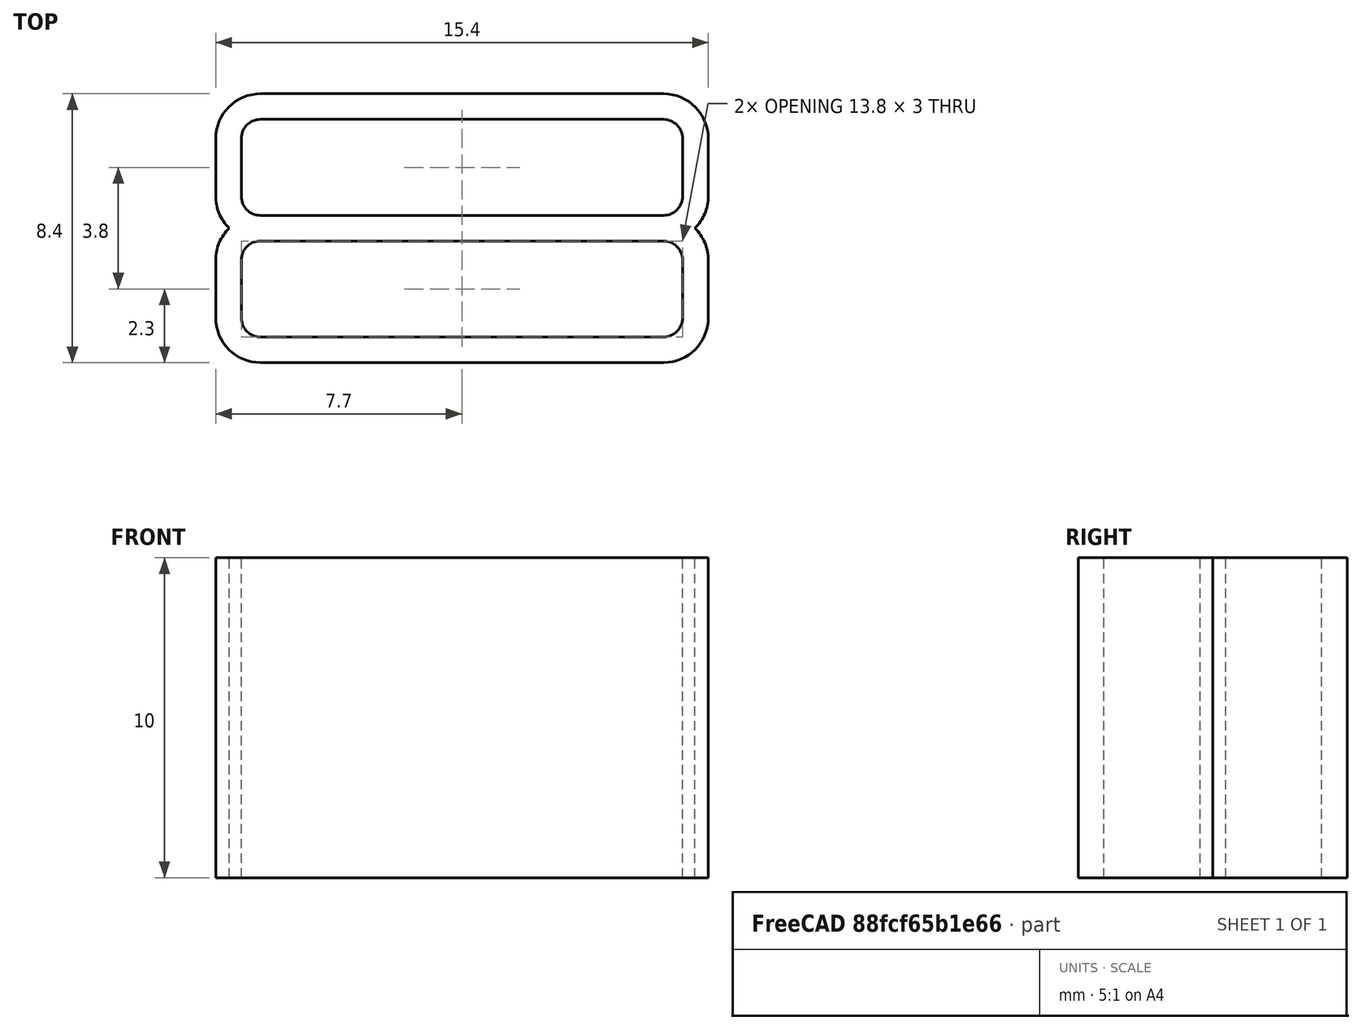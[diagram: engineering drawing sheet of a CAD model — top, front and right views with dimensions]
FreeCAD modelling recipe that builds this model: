
FCSTD DOCUMENT  (FreeCAD 1.0R39109 (Git))
Label: keeper
License: All rights reserved
LicenseURL: https://en.wikipedia.org/wiki/All_rights_reserved
objects: Sketcher::SketchObject×1, Spreadsheet::Sheet×1, PartDesign::Pad×1, PartDesign::Body×1
note: 6 computed .brp shape members not serialized (recipe doc carries the construction recipe); baked Part::Feature solids carry a one-line shape summary decoded from their .brp

FEATURE [Sketcher::SketchObject] Sketch
  ArcFitTolerance = 1e-06
  AttachmentSupport = -> [XY_Plane]
  FullyConstrained = true
  MakeInternals = false
  MapMode = 5
  expr: Constraints[39] = Spreadsheet.base_width
  expr: Constraints[43] = Spreadsheet.base_height
  expr: Constraints[46] = Spreadsheet.nozzle_width / 2
  expr: Constraints[50] = Spreadsheet.nozzle_width / 2
  expr: Constraints[59] = Spreadsheet.nozzle_width / 2
  expr: Constraints[60] = Spreadsheet.nozzle_width / 2
  expr: Constraints[61] = Spreadsheet.nozzle_width / 2
  expr: Constraints[62] = Spreadsheet.nozzle_width / 2
  sketch-geometry (78):
    g0: LineSegment [constr] StartX=-7.3 StartY=2.8 StartZ=0 EndX=-7.3 EndY=1 EndZ=0
    g1: LineSegment [constr] StartX=-6.3 StartY=0 StartZ=0 EndX=6.3 EndY=0 EndZ=0
    g2: LineSegment [constr] StartX=7.3 StartY=1 StartZ=0 EndX=7.3 EndY=2.8 EndZ=0
    g3: LineSegment [constr] StartX=6.3 StartY=3.8 StartZ=0 EndX=-6.3 EndY=3.8 EndZ=0
    g4: ArcOfCircle [constr] CenterX=-6.3 CenterY=2.8 CenterZ=0 NormalX=0 NormalY=0 NormalZ=1 AngleXU=0 Radius=1 StartAngle=1.5708 EndAngle=3.14159
    g5: ArcOfCircle [constr] CenterX=-6.3 CenterY=1 CenterZ=0 NormalX=0 NormalY=0 NormalZ=1 AngleXU=0 Radius=1 StartAngle=3.14159 EndAngle=4.71239
    g6: ArcOfCircle [constr] CenterX=6.3 CenterY=1 CenterZ=0 NormalX=0 NormalY=0 NormalZ=1 AngleXU=0 Radius=1 StartAngle=4.71239 EndAngle=6.28319
    g7: ArcOfCircle [constr] CenterX=6.3 CenterY=2.8 CenterZ=0 NormalX=0 NormalY=0 NormalZ=1 AngleXU=0 Radius=1 StartAngle=0 EndAngle=1.5708
    g8: GeomPoint [constr] X=-7.3 Y=3.8 Z=0
    g9: GeomPoint [constr] X=7.3 Y=0 Z=0
    g10: LineSegment [constr] StartX=-7.3 StartY=-1 StartZ=0 EndX=-7.3 EndY=-2.8 EndZ=0
    g11: LineSegment [constr] StartX=-6.3 StartY=-3.8 StartZ=0 EndX=6.3 EndY=-3.8 EndZ=0
    g12: LineSegment [constr] StartX=7.3 StartY=-2.8 StartZ=0 EndX=7.3 EndY=-1 EndZ=0
    g13: LineSegment [constr] StartX=6.3 StartY=0 StartZ=0 EndX=-6.3 EndY=0 EndZ=0
    g14: ArcOfCircle [constr] CenterX=-6.3 CenterY=-1 CenterZ=0 NormalX=0 NormalY=0 NormalZ=1 AngleXU=0 Radius=1 StartAngle=1.5708 EndAngle=3.14159
    g15: ArcOfCircle [constr] CenterX=-6.3 CenterY=-2.8 CenterZ=0 NormalX=0 NormalY=0 NormalZ=1 AngleXU=0 Radius=1 StartAngle=3.14159 EndAngle=4.71239
    g16: ArcOfCircle [constr] CenterX=6.3 CenterY=-2.8 CenterZ=0 NormalX=0 NormalY=0 NormalZ=1 AngleXU=0 Radius=1 StartAngle=4.71239 EndAngle=6.28319
    g17: ArcOfCircle [constr] CenterX=6.3 CenterY=-1 CenterZ=0 NormalX=0 NormalY=0 NormalZ=1 AngleXU=0 Radius=1 StartAngle=0 EndAngle=1.5708
    g18: GeomPoint [constr] X=-7.3 Y=0 Z=0
    g19: GeomPoint [constr] X=7.3 Y=-3.8 Z=0
    g20: LineSegment StartX=-6.3 StartY=4.2 StartZ=0 EndX=6.3 EndY=4.2 EndZ=0
    g21: LineSegment StartX=-6.3 StartY=3.4 StartZ=0 EndX=6.3 EndY=3.4 EndZ=0
    g22: LineSegment StartX=-6.3 StartY=0.4 StartZ=0 EndX=6.3 EndY=0.4 EndZ=0
    g23: LineSegment StartX=-6.3 StartY=-0.4 StartZ=0 EndX=6.3 EndY=-0.4 EndZ=0
    g24: LineSegment StartX=-6.3 StartY=-3.4 StartZ=0 EndX=6.3 EndY=-3.4 EndZ=0
    g25: LineSegment StartX=-6.3 StartY=-4.2 StartZ=0 EndX=6.3 EndY=-4.2 EndZ=0
    g26: LineSegment StartX=-7.7 StartY=2.8 StartZ=0 EndX=-7.7 EndY=1 EndZ=0
    g27: LineSegment StartX=-6.9 StartY=2.8 StartZ=0 EndX=-6.9 EndY=1 EndZ=0
    g28: LineSegment [constr] StartX=-7.7 StartY=2.8 StartZ=0 EndX=-6.9 EndY=2.8 EndZ=0
    g29: LineSegment [constr] StartX=-7.7 StartY=1 StartZ=0 EndX=-6.9 EndY=1 EndZ=0
    g30: ArcOfCircle CenterX=-6.3 CenterY=2.8 CenterZ=0 NormalX=0 NormalY=0 NormalZ=1 AngleXU=0 Radius=0.6 StartAngle=1.5708 EndAngle=3.14159
    g31: LineSegment [constr] StartX=-6.3 StartY=3.4 StartZ=0 EndX=-6.3 EndY=2.8 EndZ=0
    g32: LineSegment [constr] StartX=-6.9 StartY=2.8 StartZ=0 EndX=-6.3 EndY=2.8 EndZ=0
    g33: ArcOfCircle CenterX=-6.3 CenterY=1 CenterZ=0 NormalX=0 NormalY=0 NormalZ=1 AngleXU=0 Radius=0.6 StartAngle=3.14159 EndAngle=4.71239
    g34: LineSegment [constr] StartX=-6.3 StartY=1 StartZ=0 EndX=-6.3 EndY=0.4 EndZ=0
    g35: LineSegment [constr] StartX=-6.9 StartY=1 StartZ=0 EndX=-6.3 EndY=1 EndZ=0
    g36: ArcOfCircle CenterX=-6.3 CenterY=2.8 CenterZ=0 NormalX=0 NormalY=0 NormalZ=1 AngleXU=0 Radius=1.4 StartAngle=1.5708 EndAngle=3.14159
    g37: LineSegment [constr] StartX=-6.3 StartY=4.2 StartZ=0 EndX=-6.3 EndY=2.8 EndZ=0
    g38: LineSegment [constr] StartX=-7.7 StartY=2.8 StartZ=0 EndX=-6.3 EndY=2.8 EndZ=0
    g39: LineSegment StartX=-7.7 StartY=-1 StartZ=0 EndX=-7.7 EndY=-2.8 EndZ=0
    g40: LineSegment StartX=-6.9 StartY=-1 StartZ=0 EndX=-6.9 EndY=-2.8 EndZ=0
    g41: LineSegment [constr] StartX=-7.7 StartY=-1 StartZ=0 EndX=-6.9 EndY=-1 EndZ=0
    g42: LineSegment [constr] StartX=-7.7 StartY=-2.8 StartZ=0 EndX=-6.9 EndY=-2.8 EndZ=0
    g43: ArcOfCircle CenterX=-6.3 CenterY=-1 CenterZ=0 NormalX=0 NormalY=0 NormalZ=1 AngleXU=0 Radius=0.6 StartAngle=1.5708 EndAngle=3.14159
    g44: LineSegment [constr] StartX=-6.3 StartY=-0.4 StartZ=0 EndX=-6.3 EndY=-1 EndZ=0
    g45: LineSegment [constr] StartX=-6.9 StartY=-1 StartZ=0 EndX=-6.3 EndY=-1 EndZ=0
    g46: ArcOfCircle [constr] CenterX=-6.3 CenterY=-1 CenterZ=0 NormalX=0 NormalY=0 NormalZ=1 AngleXU=0 Radius=1.4 StartAngle=1.5708 EndAngle=3.14159
    g47: ArcOfCircle [constr] CenterX=-6.3 CenterY=1 CenterZ=0 NormalX=0 NormalY=0 NormalZ=1 AngleXU=0 Radius=1.4 StartAngle=3.14159 EndAngle=4.71239
    g48: LineSegment [constr] StartX=-6.9 StartY=-2.8 StartZ=0 EndX=-6.3 EndY=-2.8 EndZ=0
    g49: LineSegment [constr] StartX=-6.3 StartY=-3.4 StartZ=0 EndX=-6.3 EndY=-2.8 EndZ=0
    g50: ArcOfCircle CenterX=-6.3 CenterY=-2.8 CenterZ=0 NormalX=0 NormalY=0 NormalZ=1 AngleXU=0 Radius=0.6 StartAngle=3.14159 EndAngle=4.71239
    g51: ArcOfCircle CenterX=-6.3 CenterY=-2.8 CenterZ=0 NormalX=0 NormalY=0 NormalZ=1 AngleXU=0 Radius=1.4 StartAngle=3.14159 EndAngle=4.71239
    g52: LineSegment StartX=6.9 StartY=2.8 StartZ=0 EndX=6.9 EndY=1 EndZ=0
    g53: LineSegment [constr] StartX=6.9 StartY=2.8 StartZ=0 EndX=7.7 EndY=2.8 EndZ=0
    g54: LineSegment [constr] StartX=6.3 StartY=3.4 StartZ=0 EndX=6.3 EndY=2.8 EndZ=0
    g55: LineSegment [constr] StartX=6.3 StartY=2.8 StartZ=0 EndX=6.9 EndY=2.8 EndZ=0
    g56: ArcOfCircle CenterX=6.3 CenterY=2.8 CenterZ=0 NormalX=0 NormalY=0 NormalZ=1 AngleXU=0 Radius=0.6 StartAngle=4.3e-15 EndAngle=1.5708
    g57: ArcOfCircle CenterX=6.3 CenterY=2.8 CenterZ=0 NormalX=0 NormalY=0 NormalZ=1 AngleXU=0 Radius=1.4 StartAngle=2.9e-15 EndAngle=1.5708
    g58: LineSegment [constr] StartX=6.9 StartY=1 StartZ=0 EndX=6.3 EndY=1 EndZ=0
    g59: LineSegment [constr] StartX=6.3 StartY=0.4 StartZ=0 EndX=6.3 EndY=1 EndZ=0
    g60: ArcOfCircle CenterX=6.3 CenterY=1 CenterZ=0 NormalX=0 NormalY=0 NormalZ=1 AngleXU=0 Radius=0.6 StartAngle=4.71239 EndAngle=6.28319
    g61: LineSegment StartX=6.9 StartY=-1 StartZ=0 EndX=6.9 EndY=-2.8 EndZ=0
    g62: LineSegment StartX=7.7 StartY=-1 StartZ=0 EndX=7.7 EndY=-2.8 EndZ=0
    g63: LineSegment [constr] StartX=6.9 StartY=-1 StartZ=0 EndX=7.7 EndY=-1 EndZ=0
    g64: LineSegment [constr] StartX=6.3 StartY=-3.4 StartZ=0 EndX=6.3 EndY=-2.8 EndZ=0
    g65: LineSegment [constr] StartX=6.9 StartY=-2.8 StartZ=0 EndX=6.3 EndY=-2.8 EndZ=0
    g66: ArcOfCircle CenterX=6.3 CenterY=-2.8 CenterZ=0 NormalX=0 NormalY=0 NormalZ=1 AngleXU=0 Radius=0.6 StartAngle=4.71239 EndAngle=6.28319
    g67: ArcOfCircle CenterX=6.3 CenterY=-2.8 CenterZ=0 NormalX=0 NormalY=0 NormalZ=1 AngleXU=0 Radius=1.4 StartAngle=4.71239 EndAngle=6.28319
    g68: LineSegment [constr] StartX=6.3 StartY=-0.4 StartZ=0 EndX=6.3 EndY=-1 EndZ=0
    g69: LineSegment [constr] StartX=6.9 StartY=-1 StartZ=0 EndX=6.3 EndY=-1 EndZ=0
    g70: ArcOfCircle CenterX=6.3 CenterY=-1 CenterZ=0 NormalX=0 NormalY=0 NormalZ=1 AngleXU=0 Radius=0.6 StartAngle=0 EndAngle=1.5708
    g71: ArcOfCircle [constr] CenterX=6.3 CenterY=1 CenterZ=0 NormalX=0 NormalY=0 NormalZ=1 AngleXU=0 Radius=1.4 StartAngle=4.71239 EndAngle=6.28319
    g72: ArcOfCircle [constr] CenterX=6.3 CenterY=-1 CenterZ=0 NormalX=0 NormalY=0 NormalZ=1 AngleXU=0 Radius=1.4 StartAngle=5e-16 EndAngle=1.5708
    g73: ArcOfCircle CenterX=6.3 CenterY=-1 CenterZ=0 NormalX=0 NormalY=0 NormalZ=1 AngleXU=0 Radius=1.4 StartAngle=5e-16 EndAngle=0.795603
    g74: LineSegment StartX=7.7 StartY=2.8 StartZ=0 EndX=7.7 EndY=1 EndZ=0
    g75: ArcOfCircle CenterX=6.3 CenterY=1 CenterZ=0 NormalX=0 NormalY=0 NormalZ=1 AngleXU=0 Radius=1.4 StartAngle=5.48758 EndAngle=6.28319
    g76: ArcOfCircle CenterX=-6.3 CenterY=1 CenterZ=0 NormalX=0 NormalY=0 NormalZ=1 AngleXU=0 Radius=1.4 StartAngle=3.14159 EndAngle=3.9372
    g77: ArcOfCircle CenterX=-6.3 CenterY=-1 CenterZ=0 NormalX=0 NormalY=0 NormalZ=1 AngleXU=0 Radius=1.4 StartAngle=2.34599 EndAngle=3.14159
  constraints (191):
    c: Tangent(g0,g4) = -1.5708
    c: Tangent(g0,g5) = -1.5708
    c: Tangent(g1,g5) = -1.5708
    c: Tangent(g1,g6) = -1.5708
    c: Tangent(g2,g6) = -1.5708
    c: Tangent(g2,g7) = -1.5708
    c: Tangent(g3,g7) = -1.5708
    c: Tangent(g3,g4) = -1.5708
    c: Vertical(g0)
    c: Vertical(g2)
    c: Horizontal(g1)
    c: Horizontal(g3)
    c: Equal(g4,g5)
    c: Equal(g5,g6)
    c: PointOnObject(g8,g0)
    c: PointOnObject(g8,g3)
    c: PointOnObject(g9,g1)
    c: PointOnObject(g9,g2)
    c: Radius(g5) = 1
    c: Tangent(g10,g14) = -1.5708
    c: Tangent(g10,g15) = -1.5708
    c: Tangent(g11,g15) = -1.5708
    c: Tangent(g11,g16) = -1.5708
    c: Tangent(g12,g16) = -1.5708
    c: Tangent(g12,g17) = -1.5708
    c: Tangent(g13,g17) = -1.5708
    c: Tangent(g13,g14) = -1.5708
    c: Vertical(g10)
    c: Vertical(g12)
    c: Horizontal(g11)
    c: Horizontal(g13)
    c: Equal(g14,g15)
    c: Equal(g15,g16)
    c: Equal(g16,g17)
    c: PointOnObject(g18,g10)
    c: PointOnObject(g18,g13)
    c: PointOnObject(g19,g11)
    c: PointOnObject(g19,g12)
    c: Radius(g15) = 1
    c: DistanceX(g0,g2) = 14.6
    c: Coincident(g13,g1)
    c: Equal(g12,g2)
    c: Symmetric(g3,g11,g-1)
    c: DistanceY(g11,g3) = 7.6
    c: Symmetric(g0,g2,g-2)
    c: Equal(g20,g3)
    c: DistanceY(g3,g20) = 0.4
    c: Symmetric(g20,g20,g-2)
    c: Equal(g21,g20)
    c: Symmetric(g21,g21,g-2)
    c: DistanceY(g21,g3) = 0.4
    c: Equal(g21,g22)
    c: Equal(g22,g23)
    c: Equal(g23,g24)
    c: Equal(g24,g25)
    c: Symmetric(g22,g22,g-2)
    c: Symmetric(g23,g23,g-2)
    c: Symmetric(g24,g24,g-2)
    c: Symmetric(g25,g25,g-2)
    c: DistanceY(g1,g22) = 0.4
    c: DistanceY(g23,g1) = 0.4
    c: DistanceY(g11,g24) = 0.4
    c: DistanceY(g25,g11) = 0.4
    c: Vertical(g26)
    c: Vertical(g27)
    c: Equal(g26,g27)
    c: Symmetric(g26,g27,g0)
    c: Coincident(g28,g26)
    c: Coincident(g28,g27)
    c: PointOnObject(g0,g28)
    c: Coincident(g29,g26)
    c: Coincident(g29,g27)
    c: PointOnObject(g0,g29)
    c: Coincident(g30,g27)
    c: Coincident(g30,g21)
    c: Coincident(g31,g21)
    c: Coincident(g31,g30)
    c: Vertical(g31)
    c: Coincident(g32,g27)
    c: Coincident(g32,g4)
    c: Coincident(g33,g27)
    c: Coincident(g33,g22)
    c: Coincident(g34,g33)
    c: Coincident(g34,g22)
    c: Coincident(g35,g27)
    c: Coincident(g35,g33)
    c: Perpendicular(g34,g35)
    c: Coincident(g36,g20)
    c: Coincident(g36,g26)
    c: Coincident(g37,g20)
    c: Coincident(g37,g36)
    c: Coincident(g38,g26)
    c: Coincident(g38,g36)
    c: Perpendicular(g37,g38)
    c: Vertical(g40)
    c: Equal(g39,g40)
    c: Symmetric(g39,g40,g10)
    c: Coincident(g41,g39)
    c: Coincident(g41,g40)
    c: PointOnObject(g10,g41)
    c: Coincident(g42,g39)
    c: Coincident(g42,g40)
    c: PointOnObject(g10,g42)
    c: Coincident(g43,g23)
    c: Coincident(g43,g40)
    c: Coincident(g44,g23)
    c: Coincident(g44,g43)
    c: Coincident(g45,g40)
    c: Coincident(g45,g43)
    c: Coincident(g46,g14)
    c: Coincident(g46,g39)
    c: Coincident(g46,g22)
    c: Coincident(g47,g5)
    c: Coincident(g47,g26)
    c: Coincident(g47,g23)
    c: Coincident(g48,g40)
    c: Coincident(g49,g24)
    c: Coincident(g49,g48)
    c: Coincident(g50,g48)
    c: Coincident(g50,g40)
    c: Coincident(g50,g24)
    c: Perpendicular(g49,g48)
    c: Coincident(g51,g15)
    c: Coincident(g51,g39)
    c: Coincident(g51,g25)
    c: Vertical(g52)
    c: Symmetric(g52,g53,g2)
    c: Coincident(g53,g52)
    c: PointOnObject(g2,g53)
    c: Coincident(g54,g21)
    c: Coincident(g55,g54)
    c: Coincident(g55,g52)
    c: Coincident(g56,g54)
    c: Coincident(g56,g21)
    c: Coincident(g56,g52)
    c: Perpendicular(g54,g55)
    c: Coincident(g58,g52)
    c: Coincident(g59,g22)
    c: Coincident(g59,g58)
    c: Coincident(g60,g58)
    c: Coincident(g60,g52)
    c: Coincident(g60,g22)
    c: Perpendicular(g59,g58)
    c: Vertical(g61)
    c: Equal(g61,g62)
    c: Symmetric(g61,g62,g12)
    c: Equal(g12,g61)
    c: Coincident(g63,g61)
    c: Coincident(g63,g62)
    c: PointOnObject(g12,g63)
    c: Coincident(g64,g24)
    c: Coincident(g65,g61)
    c: Coincident(g65,g64)
    c: Coincident(g66,g64)
    c: Coincident(g66,g61)
    c: Coincident(g66,g24)
    c: Perpendicular(g64,g65)
    c: Coincident(g67,g16)
    c: Coincident(g67,g62)
    c: Coincident(g67,g25)
    c: Coincident(g68,g23)
    c: Coincident(g69,g61)
    c: Coincident(g69,g68)
    c: Horizontal(g69)
    c: Coincident(g70,g68)
    c: Coincident(g70,g23)
    c: Coincident(g70,g61)
    c: Coincident(g71,g6)
    c: Coincident(g71,g23)
    c: Coincident(g72,g17)
    c: Coincident(g72,g62)
    c: Coincident(g72,g22)
    c: Coincident(g73,g17)
    c: Coincident(g73,g62)
    c: Coincident(g57,g53)
    c: Coincident(g74,g53)
    c: Coincident(g74,g71)
    c: Equal(g52,g74)
    c: Equal(g52,g61)
    c: Coincident(g75,g6)
    c: Coincident(g75,g71)
    c: Coincident(g75,g73)
    c: Coincident(g20,g57)
    c: Coincident(g57,g7)
    c: Perpendicular(g44,g45)
    c: Coincident(g76,g5)
    c: Coincident(g76,g26)
    c: PointOnObject(g76,g46)
    c: Coincident(g77,g14)
    c: Coincident(g77,g39)
    c: PointOnObject(g77,g-1)
FEATURE [Spreadsheet::Sheet] Spreadsheet
  cells = A1='base_height; B1(base_height)==6 + 2 * B4; A2='base_width; B2(base_width)=14.6; A3='depth; B3(depth)=10; A4='nozzle_width; B4(nozzle_width)=0.8
FEATURE [PartDesign::Pad] Pad
  Direction = (0,0,1)
  Length = 10
  Length2 = 10
  Profile = -> Sketch
  ReferenceAxis = -> Sketch [N_Axis]
  Refine = true
  Suppressed = false
  Type = 0
  expr: Length = Spreadsheet.depth
FEATURE [PartDesign::Body] Body
  AllowCompound = false
  Group = -> [Sketch,Pad]
  Origin = -> Origin
  Tip = -> Pad
